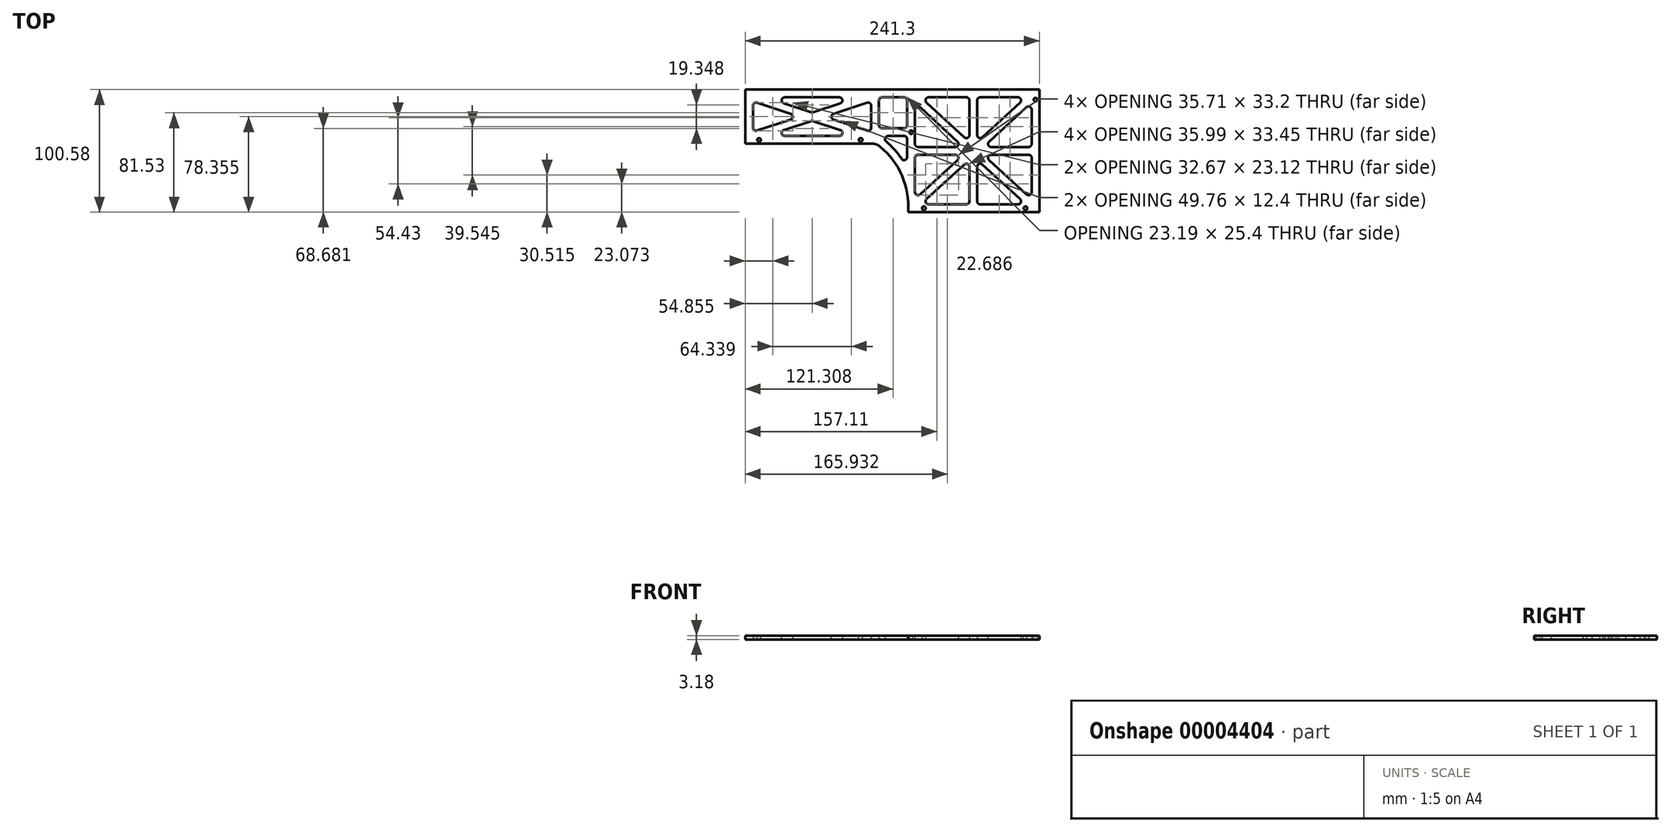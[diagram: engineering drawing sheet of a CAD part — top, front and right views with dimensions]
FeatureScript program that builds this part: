
annotation { "Feature Type Name" : "Feature", "Feature Type Description" : "" }
export const myFeature = defineFeature(function(context is Context, id is Id, definition is map)
    precondition{}
    {
        {
            var Q0;
            Q0=qCreatedBy(makeId("Top.planeOp"),FACE);
            var sketch = newSketch(context, id + "F0", { "sketchPlane" : qUnion([Q0])});
            skLineSegment(sketch, "E0", {"start": v(0, 0) * mm, "end": v(241.3, 0) * mm});
            skLineSegment(sketch, "E1", {"start": v(241.3, 0) * mm, "end": v(241.3, -100.58) * mm});
            skLineSegment(sketch, "E2", {"start": v(241.3, -100.58) * mm, "end": v(133.6, -100.58) * mm});
            skLineSegment(sketch, "E3", {"start": v(107.7, -44.45) * mm, "end": v(0, -44.45) * mm});
            skLineSegment(sketch, "E4", {"start": v(0, -44.45) * mm, "end": v(0, 0) * mm});
            skLineSegment(sketch, "E5.0", {"start": v(6.35, -34.76) * mm, "end": v(6.35, -9.7) * mm});
            skLineSegment(sketch, "E5.1", {"start": v(93.15, -38.1) * mm, "end": v(16.56, -38.1) * mm});
            skLineSegment(sketch, "E5.3", {"start": v(230.26, -94.23) * mm, "end": v(190.28, -94.23) * mm});
            skLineSegment(sketch, "E5.4", {"start": v(234.95, -10.66) * mm, "end": v(234.95, -47.12) * mm});
            skLineSegment(sketch, "E5.5", {"start": v(16.56, -6.35) * mm, "end": v(93.15, -6.35) * mm});
            skLineSegment(sketch, "E6", {"start": v(132.9, -64.8) * mm, "end": v(132.9, -38.1) * mm});
            skLineSegment(sketch, "E7", {"start": v(109.71, -31.75) * mm, "end": v(109.71, -6.35) * mm});
            skLineSegment(sketch, "E8.0", {"start": v(139.26, -89.92) * mm, "end": v(139.26, -53.47) * mm});
            skLineSegment(sketch, "E9.0", {"start": v(103.36, -34.76) * mm, "end": v(103.36, -9.7) * mm});
            skLineSegment(sketch, "E10.trimOffspring", {"start": v(143.95, -6.35) * mm, "end": v(183.93, -6.35) * mm});
            skLineSegment(sketch, "E11.trimOffspring", {"start": v(109.71, -6.35) * mm, "end": v(132.9, -6.35) * mm});
            skLineSegment(sketch, "E12", {"start": v(109.71, -38.1) * mm, "end": v(132.9, -38.1) * mm});
            skLineSegment(sketch, "E13.0", {"start": v(109.71, -31.75) * mm, "end": v(132.9, -31.75) * mm});
            skLineSegment(sketch, "E14.trimOffspring", {"start": v(132.9, -31.75) * mm, "end": v(132.9, -6.35) * mm});
            skLineSegment(sketch, "E15", {"start": v(234.95, -94.23) * mm, "end": v(139.26, -6.35) * mm, "construction": true});
            skLineSegment(sketch, "E16", {"start": v(139.26, -94.23) * mm, "end": v(234.95, -6.35) * mm, "construction": true});
            skLineSegment(sketch, "E17.0", {"start": v(234.95, -89.92) * mm, "end": v(195.25, -53.47) * mm});
            skLineSegment(sketch, "E18.0", {"start": v(230.26, -94.23) * mm, "end": v(190.28, -57.52) * mm});
            skLineSegment(sketch, "E19.0", {"start": v(143.95, -94.23) * mm, "end": v(183.93, -57.52) * mm});
            skLineSegment(sketch, "E20.0", {"start": v(139.26, -89.92) * mm, "end": v(178.95, -53.47) * mm});
            skLineSegment(sketch, "E21.trimOffspring", {"start": v(183.93, -43.07) * mm, "end": v(143.95, -6.35) * mm});
            skLineSegment(sketch, "E22.trimOffspring", {"start": v(195.25, -47.12) * mm, "end": v(234.95, -10.66) * mm});
            skLineSegment(sketch, "E23.trimOffspring", {"start": v(178.95, -47.12) * mm, "end": v(139.26, -10.66) * mm});
            skLineSegment(sketch, "E24.trimOffspring", {"start": v(190.28, -43.07) * mm, "end": v(230.26, -6.35) * mm});
            skLineSegment(sketch, "E25", {"start": v(234.95, -50.3) * mm, "end": v(139.26, -50.3) * mm, "construction": true});
            skLineSegment(sketch, "E26", {"start": v(187.1, -94.23) * mm, "end": v(187.1, -6.35) * mm, "construction": true});
            skLineSegment(sketch, "E27.0", {"start": v(190.28, -94.23) * mm, "end": v(190.28, -57.52) * mm});
            skLineSegment(sketch, "E28.0", {"start": v(183.93, -94.23) * mm, "end": v(183.93, -57.52) * mm});
            skLineSegment(sketch, "E29.0", {"start": v(234.95, -47.12) * mm, "end": v(195.25, -47.12) * mm});
            skLineSegment(sketch, "E30.0", {"start": v(234.95, -53.47) * mm, "end": v(195.25, -53.47) * mm});
            skLineSegment(sketch, "E31.trimOffspring", {"start": v(190.28, -43.07) * mm, "end": v(190.28, -6.35) * mm});
            skLineSegment(sketch, "E32.trimOffspring", {"start": v(183.93, -43.07) * mm, "end": v(183.93, -6.35) * mm});
            skLineSegment(sketch, "E33.trimOffspring", {"start": v(178.95, -47.12) * mm, "end": v(139.26, -47.12) * mm});
            skLineSegment(sketch, "E34.trimOffspring", {"start": v(178.95, -53.47) * mm, "end": v(139.26, -53.47) * mm});
            skLineSegment(sketch, "E35.trimOffspring", {"start": v(183.93, -94.23) * mm, "end": v(143.95, -94.23) * mm});
            skLineSegment(sketch, "E36.trimOffspring", {"start": v(139.26, -47.12) * mm, "end": v(139.26, -10.66) * mm});
            skLineSegment(sketch, "E37.trimOffspring", {"start": v(190.28, -6.35) * mm, "end": v(230.26, -6.35) * mm});
            skLineSegment(sketch, "E38.trimOffspring", {"start": v(234.95, -53.47) * mm, "end": v(234.95, -89.92) * mm});
            skLineSegment(sketch, "E39", {"start": v(103.36, -38.1) * mm, "end": v(6.35, -6.35) * mm, "construction": true});
            skLineSegment(sketch, "E40", {"start": v(6.35, -38.1) * mm, "end": v(103.36, -6.35) * mm, "construction": true});
            skLineSegment(sketch, "E41.0", {"start": v(103.36, -34.76) * mm, "end": v(65.06, -22.23) * mm});
            skLineSegment(sketch, "E42.0", {"start": v(93.15, -38.1) * mm, "end": v(54.86, -25.57) * mm});
            skLineSegment(sketch, "E43.0", {"start": v(16.56, -38.1) * mm, "end": v(54.86, -25.57) * mm});
            skLineSegment(sketch, "E44.0", {"start": v(6.35, -34.76) * mm, "end": v(44.65, -22.23) * mm});
            skLineSegment(sketch, "E45.trimOffspring", {"start": v(54.86, -18.88) * mm, "end": v(16.56, -6.35) * mm});
            skLineSegment(sketch, "E46.trimOffspring", {"start": v(65.06, -22.23) * mm, "end": v(103.36, -9.7) * mm});
            skLineSegment(sketch, "E47.trimOffspring", {"start": v(44.65, -22.23) * mm, "end": v(6.35, -9.7) * mm});
            skLineSegment(sketch, "E48.trimOffspring", {"start": v(54.86, -18.88) * mm, "end": v(93.15, -6.35) * mm});
            skArc(sketch, "E49", {"start": v(133.6, -100.58) * mm, "mid": v(127.94, -69.15) * mm, "end": v(107.7, -44.45) * mm});
            skArc(sketch, "E50.0", {"start": v(132.9, -64.8) * mm, "mid": v(123.03, -49.96) * mm, "end": v(109.71, -38.1) * mm});
            skSolve(sketch);
        }
        {
            var Q0;
            Q0=makeQuery(id+"F0.imprint","IMPRINT",FACE,{"disambiguationData":[TD([[makeQuery(id+"F0.imprint","IMPRINT",EDGE,{"derivedFrom":sQuery(id+"F0.wireOp",EDGE,"E0")}),-1.0]])]});
            extrude(context, id + "F1", {"entities" : qUnion([Q0]), "depth" : 3.17 * mm});
        }
        {
            var Q0;
            Q0=makeQuery(id+"F1.opExtrude","SWEPT_EDGE",EDGE,{"disambiguationData":[OSD([sQuery(id+"F0.wireOp",EDGE,"E6"),sQuery(id+"F0.wireOp",EDGE,"E50.0")])]});
            var Q1;
            Q1=makeQuery(id+"F1.opExtrude","SWEPT_EDGE",EDGE,{"disambiguationData":[OSD([sQuery(id+"F0.wireOp",EDGE,"E17.0"),sQuery(id+"F0.wireOp",EDGE,"E38.trimOffspring")])]});
            var Q2;
            Q2=makeQuery(id+"F1.opExtrude","SWEPT_EDGE",EDGE,{"disambiguationData":[OSD([sQuery(id+"F0.wireOp",EDGE,"E28.0"),sQuery(id+"F0.wireOp",EDGE,"E35.trimOffspring")])]});
            var Q3;
            Q3=makeQuery(id+"F1.opExtrude","SWEPT_EDGE",EDGE,{"disambiguationData":[OSD([sQuery(id+"F0.wireOp",EDGE,"E21.trimOffspring"),sQuery(id+"F0.wireOp",EDGE,"E32.trimOffspring")])]});
            var Q4;
            Q4=makeQuery(id+"F1.opExtrude","SWEPT_EDGE",EDGE,{"disambiguationData":[OSD([sQuery(id+"F0.wireOp",EDGE,"E5.4"),sQuery(id+"F0.wireOp",EDGE,"E29.0")])]});
            var Q5;
            Q5=makeQuery(id+"F1.opExtrude","SWEPT_EDGE",EDGE,{"disambiguationData":[OSD([sQuery(id+"F0.wireOp",EDGE,"E6"),sQuery(id+"F0.wireOp",EDGE,"E50.0")])]});
            var Q6;
            Q6=makeQuery(id+"F1.opExtrude","SWEPT_EDGE",EDGE,{"disambiguationData":[OSD([sQuery(id+"F0.wireOp",EDGE,"E6"),sQuery(id+"F0.wireOp",EDGE,"E12")])]});
            var Q7;
            Q7=makeQuery(id+"F1.opExtrude","SWEPT_EDGE",EDGE,{"disambiguationData":[OSD([sQuery(id+"F0.wireOp",EDGE,"E13.0"),sQuery(id+"F0.wireOp",EDGE,"E14.trimOffspring")])]});
            var Q8;
            Q8=makeQuery(id+"F1.opExtrude","SWEPT_EDGE",EDGE,{"disambiguationData":[OSD([sQuery(id+"F0.wireOp",EDGE,"E9.0"),sQuery(id+"F0.wireOp",EDGE,"E41.0")])]});
            var Q9;
            Q9=makeQuery(id+"F1.opExtrude","SWEPT_EDGE",EDGE,{"disambiguationData":[OSD([sQuery(id+"F0.wireOp",EDGE,"E45.trimOffspring"),sQuery(id+"F0.wireOp",EDGE,"E48.trimOffspring")])]});
            var Q10;
            Q10=makeQuery(id+"F1.opExtrude","SWEPT_EDGE",EDGE,{"disambiguationData":[OSD([sQuery(id+"F0.wireOp",EDGE,"E5.0"),sQuery(id+"F0.wireOp",EDGE,"E47.trimOffspring")])]});
            var Q11;
            Q11=makeQuery(id+"F1.opExtrude","SWEPT_EDGE",EDGE,{"disambiguationData":[OSD([sQuery(id+"F0.wireOp",EDGE,"E42.0"),sQuery(id+"F0.wireOp",EDGE,"E43.0")])]});
            var Q12;
            Q12=makeQuery(id+"F1.opExtrude","SWEPT_EDGE",EDGE,{"disambiguationData":[OSD([sQuery(id+"F0.wireOp",EDGE,"E7"),sQuery(id+"F0.wireOp",EDGE,"E11.trimOffspring")])]});
            var Q13;
            Q13=makeQuery(id+"F1.opExtrude","SWEPT_EDGE",EDGE,{"disambiguationData":[OSD([sQuery(id+"F0.wireOp",EDGE,"E10.trimOffspring"),sQuery(id+"F0.wireOp",EDGE,"E21.trimOffspring")])]});
            var Q14;
            Q14=makeQuery(id+"F1.opExtrude","SWEPT_EDGE",EDGE,{"disambiguationData":[OSD([sQuery(id+"F0.wireOp",EDGE,"E31.trimOffspring"),sQuery(id+"F0.wireOp",EDGE,"E37.trimOffspring")])]});
            var Q15;
            Q15=makeQuery(id+"F1.opExtrude","SWEPT_EDGE",EDGE,{"disambiguationData":[OSD([sQuery(id+"F0.wireOp",EDGE,"E17.0"),sQuery(id+"F0.wireOp",EDGE,"E30.0")])]});
            var Q16;
            Q16=makeQuery(id+"F1.opExtrude","SWEPT_EDGE",EDGE,{"disambiguationData":[OSD([sQuery(id+"F0.wireOp",EDGE,"E8.0"),sQuery(id+"F0.wireOp",EDGE,"E34.trimOffspring")])]});
            var Q17;
            Q17=makeQuery(id+"F1.opExtrude","SWEPT_EDGE",EDGE,{"disambiguationData":[OSD([sQuery(id+"F0.wireOp",EDGE,"E41.0"),sQuery(id+"F0.wireOp",EDGE,"E46.trimOffspring")])]});
            var Q18;
            Q18=makeQuery(id+"F1.opExtrude","SWEPT_EDGE",EDGE,{"disambiguationData":[OSD([sQuery(id+"F0.wireOp",EDGE,"E33.trimOffspring"),sQuery(id+"F0.wireOp",EDGE,"E36.trimOffspring")])]});
            var Q19;
            Q19=makeQuery(id+"F1.opExtrude","SWEPT_EDGE",EDGE,{"disambiguationData":[OSD([sQuery(id+"F0.wireOp",EDGE,"E22.trimOffspring"),sQuery(id+"F0.wireOp",EDGE,"E29.0")])]});
            var Q20;
            Q20=makeQuery(id+"F1.opExtrude","SWEPT_EDGE",EDGE,{"disambiguationData":[OSD([sQuery(id+"F0.wireOp",EDGE,"E19.0"),sQuery(id+"F0.wireOp",EDGE,"E35.trimOffspring")])]});
            var Q21;
            Q21=makeQuery(id+"F1.opExtrude","SWEPT_EDGE",EDGE,{"disambiguationData":[OSD([sQuery(id+"F0.wireOp",EDGE,"E5.3"),sQuery(id+"F0.wireOp",EDGE,"E27.0")])]});
            var Q22;
            Q22=makeQuery(id+"F1.opExtrude","SWEPT_EDGE",EDGE,{"disambiguationData":[OSD([sQuery(id+"F0.wireOp",EDGE,"E7"),sQuery(id+"F0.wireOp",EDGE,"E13.0")])]});
            var Q23;
            Q23=makeQuery(id+"F1.opExtrude","SWEPT_EDGE",EDGE,{"disambiguationData":[OSD([sQuery(id+"F0.wireOp",EDGE,"E5.1"),sQuery(id+"F0.wireOp",EDGE,"E43.0")])]});
            var Q24;
            Q24=makeQuery(id+"F1.opExtrude","SWEPT_EDGE",EDGE,{"disambiguationData":[OSD([sQuery(id+"F0.wireOp",EDGE,"E5.0"),sQuery(id+"F0.wireOp",EDGE,"E44.0")])]});
            var Q25;
            Q25=makeQuery(id+"F1.opExtrude","SWEPT_EDGE",EDGE,{"disambiguationData":[OSD([sQuery(id+"F0.wireOp",EDGE,"E8.0"),sQuery(id+"F0.wireOp",EDGE,"E20.0")])]});
            var Q26;
            Q26=makeQuery(id+"F1.opExtrude","SWEPT_EDGE",EDGE,{"disambiguationData":[OSD([sQuery(id+"F0.wireOp",EDGE,"E24.trimOffspring"),sQuery(id+"F0.wireOp",EDGE,"E31.trimOffspring")])]});
            var Q27;
            Q27=makeQuery(id+"F1.opExtrude","SWEPT_EDGE",EDGE,{"disambiguationData":[OSD([sQuery(id+"F0.wireOp",EDGE,"E9.0"),sQuery(id+"F0.wireOp",EDGE,"E46.trimOffspring")])]});
            var Q28;
            Q28=makeQuery(id+"F1.opExtrude","SWEPT_EDGE",EDGE,{"disambiguationData":[OSD([sQuery(id+"F0.wireOp",EDGE,"E11.trimOffspring"),sQuery(id+"F0.wireOp",EDGE,"E14.trimOffspring")])]});
            var Q29;
            Q29=makeQuery(id+"F1.opExtrude","SWEPT_EDGE",EDGE,{"disambiguationData":[OSD([sQuery(id+"F0.wireOp",EDGE,"E5.4"),sQuery(id+"F0.wireOp",EDGE,"E22.trimOffspring")])]});
            var Q30;
            Q30=makeQuery(id+"F1.opExtrude","SWEPT_EDGE",EDGE,{"disambiguationData":[OSD([sQuery(id+"F0.wireOp",EDGE,"E19.0"),sQuery(id+"F0.wireOp",EDGE,"E28.0")])]});
            var Q31;
            Q31=makeQuery(id+"F1.opExtrude","SWEPT_EDGE",EDGE,{"disambiguationData":[OSD([sQuery(id+"F0.wireOp",EDGE,"E18.0"),sQuery(id+"F0.wireOp",EDGE,"E27.0")])]});
            var Q32;
            Q32=makeQuery(id+"F1.opExtrude","SWEPT_EDGE",EDGE,{"disambiguationData":[OSD([sQuery(id+"F0.wireOp",EDGE,"E23.trimOffspring"),sQuery(id+"F0.wireOp",EDGE,"E36.trimOffspring")])]});
            var Q33;
            Q33=makeQuery(id+"F1.opExtrude","SWEPT_EDGE",EDGE,{"disambiguationData":[OSD([sQuery(id+"F0.wireOp",EDGE,"E5.5"),sQuery(id+"F0.wireOp",EDGE,"E45.trimOffspring")])]});
            var Q34;
            Q34=makeQuery(id+"F1.opExtrude","SWEPT_EDGE",EDGE,{"disambiguationData":[OSD([sQuery(id+"F0.wireOp",EDGE,"E44.0"),sQuery(id+"F0.wireOp",EDGE,"E47.trimOffspring")])]});
            var Q35;
            Q35=makeQuery(id+"F1.opExtrude","SWEPT_EDGE",EDGE,{"disambiguationData":[OSD([sQuery(id+"F0.wireOp",EDGE,"E5.5"),sQuery(id+"F0.wireOp",EDGE,"E48.trimOffspring")])]});
            var Q36;
            Q36=makeQuery(id+"F1.opExtrude","SWEPT_EDGE",EDGE,{"disambiguationData":[OSD([sQuery(id+"F0.wireOp",EDGE,"E24.trimOffspring"),sQuery(id+"F0.wireOp",EDGE,"E37.trimOffspring")])]});
            var Q37;
            Q37=makeQuery(id+"F1.opExtrude","SWEPT_EDGE",EDGE,{"disambiguationData":[OSD([sQuery(id+"F0.wireOp",EDGE,"E10.trimOffspring"),sQuery(id+"F0.wireOp",EDGE,"E32.trimOffspring")])]});
            var Q38;
            Q38=makeQuery(id+"F1.opExtrude","SWEPT_EDGE",EDGE,{"disambiguationData":[OSD([sQuery(id+"F0.wireOp",EDGE,"E23.trimOffspring"),sQuery(id+"F0.wireOp",EDGE,"E33.trimOffspring")])]});
            var Q39;
            Q39=makeQuery(id+"F1.opExtrude","SWEPT_EDGE",EDGE,{"disambiguationData":[OSD([sQuery(id+"F0.wireOp",EDGE,"E5.3"),sQuery(id+"F0.wireOp",EDGE,"E18.0")])]});
            var Q40;
            Q40=makeQuery(id+"F1.opExtrude","SWEPT_EDGE",EDGE,{"disambiguationData":[OSD([sQuery(id+"F0.wireOp",EDGE,"E5.1"),sQuery(id+"F0.wireOp",EDGE,"E42.0")])]});
            var Q41;
            Q41=makeQuery(id+"F1.opExtrude","SWEPT_EDGE",EDGE,{"disambiguationData":[OSD([sQuery(id+"F0.wireOp",EDGE,"E20.0"),sQuery(id+"F0.wireOp",EDGE,"E34.trimOffspring")])]});
            var Q42;
            Q42=makeQuery(id+"F1.opExtrude","SWEPT_EDGE",EDGE,{"disambiguationData":[OSD([sQuery(id+"F0.wireOp",EDGE,"E30.0"),sQuery(id+"F0.wireOp",EDGE,"E38.trimOffspring")])]});
            var Q43;
            Q43=makeQuery(id+"F1.opExtrude","SWEPT_EDGE",EDGE,{"disambiguationData":[OSD([sQuery(id+"F0.wireOp",EDGE,"E12"),sQuery(id+"F0.wireOp",EDGE,"E50.0")])]});
            fillet(context, id + "F2", {"entities" : qUnion([Q0, Q1, Q2, Q3, Q4, Q5, Q6, Q7, Q8, Q9, Q10, Q11, Q12, Q13, Q14, Q15, Q16, Q17, Q18, Q19, Q20, Q21, Q22, Q23, Q24, Q25, Q26, Q27, Q28, Q29, Q30, Q31, Q32, Q33, Q34, Q35, Q36, Q37, Q38, Q39, Q40, Q41, Q42, Q43]), "radius" : 2.54 * mm, "tangentPropagation" : true, "allowEdgeOverflow" : false});
        }
        {
            var Q0;
            Q0=makeQuery(id+"F1.opExtrude","CAP_FACE",FACE,{"disambiguationData":[OSD([sQuery(id+"F0.wireOp",EDGE,"E0"),sQuery(id+"F0.wireOp",EDGE,"E1"),sQuery(id+"F0.wireOp",EDGE,"E2"),sQuery(id+"F0.wireOp",EDGE,"E3"),sQuery(id+"F0.wireOp",EDGE,"E4"),sQuery(id+"F0.wireOp",EDGE,"E5.0"),sQuery(id+"F0.wireOp",EDGE,"E5.1"),sQuery(id+"F0.wireOp",EDGE,"E5.3"),sQuery(id+"F0.wireOp",EDGE,"E5.4"),sQuery(id+"F0.wireOp",EDGE,"E5.5"),sQuery(id+"F0.wireOp",EDGE,"E6"),sQuery(id+"F0.wireOp",EDGE,"E7"),sQuery(id+"F0.wireOp",EDGE,"E8.0"),sQuery(id+"F0.wireOp",EDGE,"E9.0"),sQuery(id+"F0.wireOp",EDGE,"E10.trimOffspring"),sQuery(id+"F0.wireOp",EDGE,"E11.trimOffspring"),sQuery(id+"F0.wireOp",EDGE,"E12"),sQuery(id+"F0.wireOp",EDGE,"E13.0"),sQuery(id+"F0.wireOp",EDGE,"E14.trimOffspring"),sQuery(id+"F0.wireOp",EDGE,"E17.0"),sQuery(id+"F0.wireOp",EDGE,"E18.0"),sQuery(id+"F0.wireOp",EDGE,"E19.0"),sQuery(id+"F0.wireOp",EDGE,"E20.0"),sQuery(id+"F0.wireOp",EDGE,"E21.trimOffspring"),sQuery(id+"F0.wireOp",EDGE,"E22.trimOffspring"),sQuery(id+"F0.wireOp",EDGE,"E23.trimOffspring"),sQuery(id+"F0.wireOp",EDGE,"E24.trimOffspring"),sQuery(id+"F0.wireOp",EDGE,"E27.0"),sQuery(id+"F0.wireOp",EDGE,"E28.0"),sQuery(id+"F0.wireOp",EDGE,"E29.0"),sQuery(id+"F0.wireOp",EDGE,"E30.0"),sQuery(id+"F0.wireOp",EDGE,"E31.trimOffspring"),sQuery(id+"F0.wireOp",EDGE,"E32.trimOffspring"),sQuery(id+"F0.wireOp",EDGE,"E33.trimOffspring"),sQuery(id+"F0.wireOp",EDGE,"E34.trimOffspring"),sQuery(id+"F0.wireOp",EDGE,"E35.trimOffspring"),sQuery(id+"F0.wireOp",EDGE,"E36.trimOffspring"),sQuery(id+"F0.wireOp",EDGE,"E37.trimOffspring"),sQuery(id+"F0.wireOp",EDGE,"E38.trimOffspring"),sQuery(id+"F0.wireOp",EDGE,"E41.0"),sQuery(id+"F0.wireOp",EDGE,"E42.0"),sQuery(id+"F0.wireOp",EDGE,"E43.0"),sQuery(id+"F0.wireOp",EDGE,"E44.0"),sQuery(id+"F0.wireOp",EDGE,"E45.trimOffspring"),sQuery(id+"F0.wireOp",EDGE,"E46.trimOffspring"),sQuery(id+"F0.wireOp",EDGE,"E47.trimOffspring"),sQuery(id+"F0.wireOp",EDGE,"E48.trimOffspring"),sQuery(id+"F0.wireOp",EDGE,"E49"),sQuery(id+"F0.wireOp",EDGE,"E50.0")])],"isStart":false});
            var sketch = newSketch(context, id + "F3", { "sketchPlane" : qUnion([Q0])});
            skCircle(sketch, "E51", {"center": v(229.87, -97.4) * mm, "radius": 1.5 * mm});
            skCircle(sketch, "E52", {"center": v(11.43, -41.28) * mm, "radius": 1.5 * mm});
            skCircle(sketch, "E53", {"center": v(238.12, -8.25) * mm, "radius": 1.5 * mm});
            skCircle(sketch, "E54", {"center": v(146.56, -97.4) * mm, "radius": 1.5 * mm});
            skCircle(sketch, "E55", {"center": v(94.74, -41.28) * mm, "radius": 1.5 * mm});
            skSolve(sketch);
        }
        {
            var Q0;
            Q0 = qSketchRegion(id + "F3", true);
            extrude(context, id + "F4", {"entities" : qUnion([Q0]), "operationType" : NewBodyOperationType.REMOVE, "endBound" : BoundingType.THROUGH_ALL, "oppositeDirection" : true, "depth" : 25.4 * mm});
        }
        {
            var Q0;
            Q0=makeQuery(id+"F1.opExtrude","SWEPT_EDGE",EDGE,{"disambiguationData":[OSD([sQuery(id+"F0.wireOp",EDGE,"E3"),sQuery(id+"F0.wireOp",EDGE,"E49")])]});
            fillet(context, id + "F5", {"entities" : qUnion([Q0]), "radius" : 10.16 * mm, "tangentPropagation" : true, "allowEdgeOverflow" : false});
        }
        {
            var Q0;
            Q0=makeQuery(id+"F1.opExtrude","CAP_FACE",FACE,{"disambiguationData":[OSD([sQuery(id+"F0.wireOp",EDGE,"E0"),sQuery(id+"F0.wireOp",EDGE,"E1"),sQuery(id+"F0.wireOp",EDGE,"E2"),sQuery(id+"F0.wireOp",EDGE,"E3"),sQuery(id+"F0.wireOp",EDGE,"E4"),sQuery(id+"F0.wireOp",EDGE,"E5.0"),sQuery(id+"F0.wireOp",EDGE,"E5.1"),sQuery(id+"F0.wireOp",EDGE,"E5.3"),sQuery(id+"F0.wireOp",EDGE,"E5.4"),sQuery(id+"F0.wireOp",EDGE,"E5.5"),sQuery(id+"F0.wireOp",EDGE,"E6"),sQuery(id+"F0.wireOp",EDGE,"E7"),sQuery(id+"F0.wireOp",EDGE,"E8.0"),sQuery(id+"F0.wireOp",EDGE,"E9.0"),sQuery(id+"F0.wireOp",EDGE,"E10.trimOffspring"),sQuery(id+"F0.wireOp",EDGE,"E11.trimOffspring"),sQuery(id+"F0.wireOp",EDGE,"E12"),sQuery(id+"F0.wireOp",EDGE,"E13.0"),sQuery(id+"F0.wireOp",EDGE,"E14.trimOffspring"),sQuery(id+"F0.wireOp",EDGE,"E17.0"),sQuery(id+"F0.wireOp",EDGE,"E18.0"),sQuery(id+"F0.wireOp",EDGE,"E19.0"),sQuery(id+"F0.wireOp",EDGE,"E20.0"),sQuery(id+"F0.wireOp",EDGE,"E21.trimOffspring"),sQuery(id+"F0.wireOp",EDGE,"E22.trimOffspring"),sQuery(id+"F0.wireOp",EDGE,"E23.trimOffspring"),sQuery(id+"F0.wireOp",EDGE,"E24.trimOffspring"),sQuery(id+"F0.wireOp",EDGE,"E27.0"),sQuery(id+"F0.wireOp",EDGE,"E28.0"),sQuery(id+"F0.wireOp",EDGE,"E29.0"),sQuery(id+"F0.wireOp",EDGE,"E30.0"),sQuery(id+"F0.wireOp",EDGE,"E31.trimOffspring"),sQuery(id+"F0.wireOp",EDGE,"E32.trimOffspring"),sQuery(id+"F0.wireOp",EDGE,"E33.trimOffspring"),sQuery(id+"F0.wireOp",EDGE,"E34.trimOffspring"),sQuery(id+"F0.wireOp",EDGE,"E35.trimOffspring"),sQuery(id+"F0.wireOp",EDGE,"E36.trimOffspring"),sQuery(id+"F0.wireOp",EDGE,"E37.trimOffspring"),sQuery(id+"F0.wireOp",EDGE,"E38.trimOffspring"),sQuery(id+"F0.wireOp",EDGE,"E41.0"),sQuery(id+"F0.wireOp",EDGE,"E42.0"),sQuery(id+"F0.wireOp",EDGE,"E43.0"),sQuery(id+"F0.wireOp",EDGE,"E44.0"),sQuery(id+"F0.wireOp",EDGE,"E45.trimOffspring"),sQuery(id+"F0.wireOp",EDGE,"E46.trimOffspring"),sQuery(id+"F0.wireOp",EDGE,"E47.trimOffspring"),sQuery(id+"F0.wireOp",EDGE,"E48.trimOffspring"),sQuery(id+"F0.wireOp",EDGE,"E49"),sQuery(id+"F0.wireOp",EDGE,"E50.0")])],"isStart":false});
            var sketch = newSketch(context, id + "F6", { "sketchPlane" : qUnion([Q0])});
            skCircle(sketch, "E56", {"center": v(136.08, -34.93) * mm, "radius": 1.5 * mm});
            skSolve(sketch);
        }
        {
            var Q0;
            Q0 = qSketchRegion(id + "F6", true);
            extrude(context, id + "F7", {"entities" : qUnion([Q0]), "operationType" : NewBodyOperationType.REMOVE, "endBound" : BoundingType.THROUGH_ALL, "oppositeDirection" : true, "depth" : 25.4 * mm});
        }
    });
